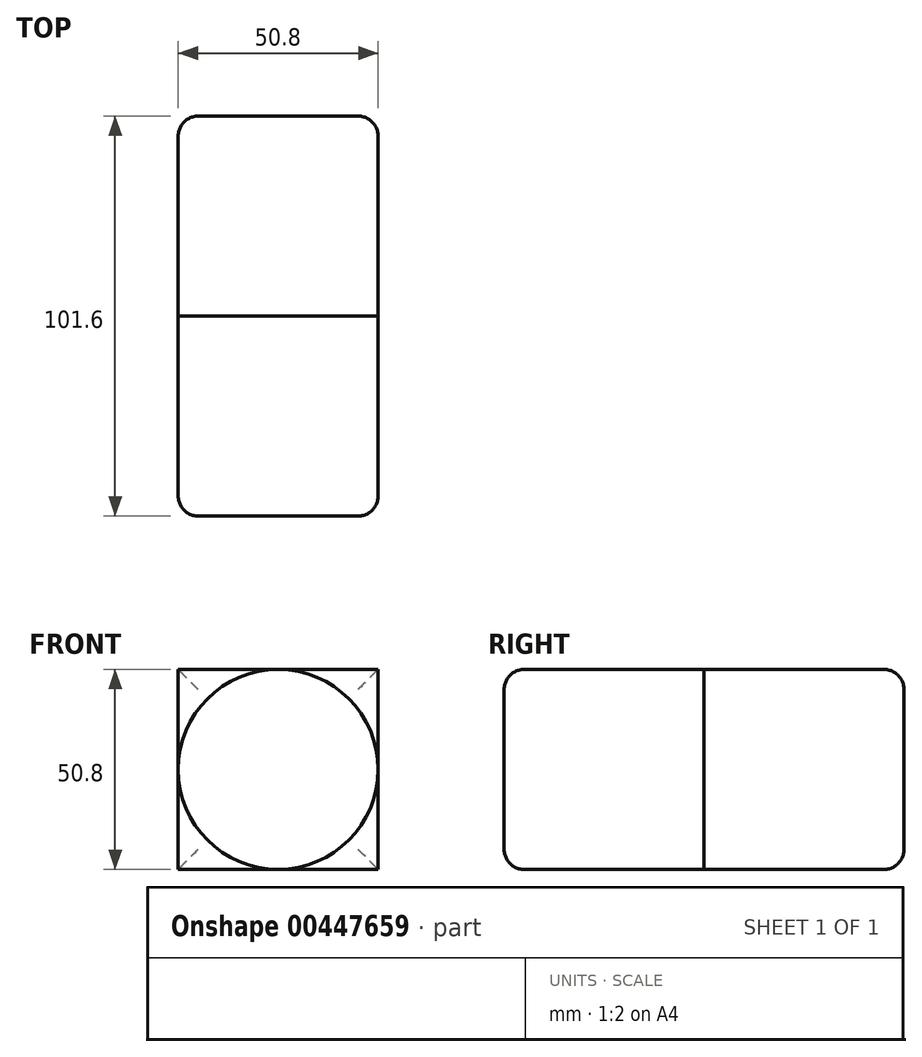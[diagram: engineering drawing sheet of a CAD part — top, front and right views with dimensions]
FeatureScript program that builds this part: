
annotation { "Feature Type Name" : "Feature", "Feature Type Description" : "" }
export const myFeature = defineFeature(function(context is Context, id is Id, definition is map)
    precondition{}
    {
        {
            var Q0;
            Q0=qCreatedBy(makeId("Front.planeOp"),FACE);
            var sketch = newSketch(context, id + "F0", { "sketchPlane" : qUnion([Q0])});
            skLineSegment(sketch, "E0.bottom", {"start": v(0, 0) * mm, "end": v(-50.8, 0) * mm});
            skLineSegment(sketch, "E0.top", {"start": v(0, 50.8) * mm, "end": v(-50.8, 50.8) * mm});
            skLineSegment(sketch, "E0.left", {"start": v(0, 0) * mm, "end": v(0, 50.8) * mm});
            skLineSegment(sketch, "E0.right", {"start": v(-50.8, 0) * mm, "end": v(-50.8, 50.8) * mm});
            skSolve(sketch);
        }
        {
            var Q0;
            Q0 = qSketchRegion(id + "F0", true);
            extrude(context, id + "F1", {"entities" : qUnion([Q0]), "depth" : 50.8 * mm});
        }
        {
            var Q0;
            Q0=makeQuery(id+"F1.opExtrude","CAP_FACE",FACE,{"disambiguationData":[OSD([sQuery(id+"F0.wireOp",EDGE,"E0.bottom"),sQuery(id+"F0.wireOp",EDGE,"E0.top"),sQuery(id+"F0.wireOp",EDGE,"E0.left"),sQuery(id+"F0.wireOp",EDGE,"E0.right")])],"isStart":false});
            var sketch = newSketch(context, id + "F2", { "sketchPlane" : qUnion([Q0])});
            skCircle(sketch, "E1", {"center": v(-25.4, 25.4) * mm, "radius": 25.4 * mm});
            skSolve(sketch);
        }
        {
            var Q0;
            Q0 = qSketchRegion(id + "F2", true);
            extrude(context, id + "F3", {"entities" : qUnion([Q0]), "operationType" : NewBodyOperationType.ADD, "depth" : 50.8 * mm});
        }
        {
            var Q0;
            Q0=makeQuery(id+"F1.opExtrude","CAP_FACE",FACE,{"disambiguationData":[OSD([sQuery(id+"F0.wireOp",EDGE,"E0.bottom"),sQuery(id+"F0.wireOp",EDGE,"E0.top"),sQuery(id+"F0.wireOp",EDGE,"E0.left"),sQuery(id+"F0.wireOp",EDGE,"E0.right")])],"isStart":true});
            fillet(context, id + "F4", {"entities" : qUnion([Q0]), "radius" : 5.08 * mm, "tangentPropagation" : true, "allowEdgeOverflow" : false});
        }
        {
            var Q0;
            Q0=makeQuery(id+"F3.opExtrude","CAP_FACE",FACE,{"disambiguationData":[OSD([sQuery(id+"F2.wireOp",EDGE,"E1")])],"isStart":false});
            fillet(context, id + "F5", {"entities" : qUnion([Q0]), "radius" : 5.08 * mm, "tangentPropagation" : true, "allowEdgeOverflow" : false});
        }
    });
